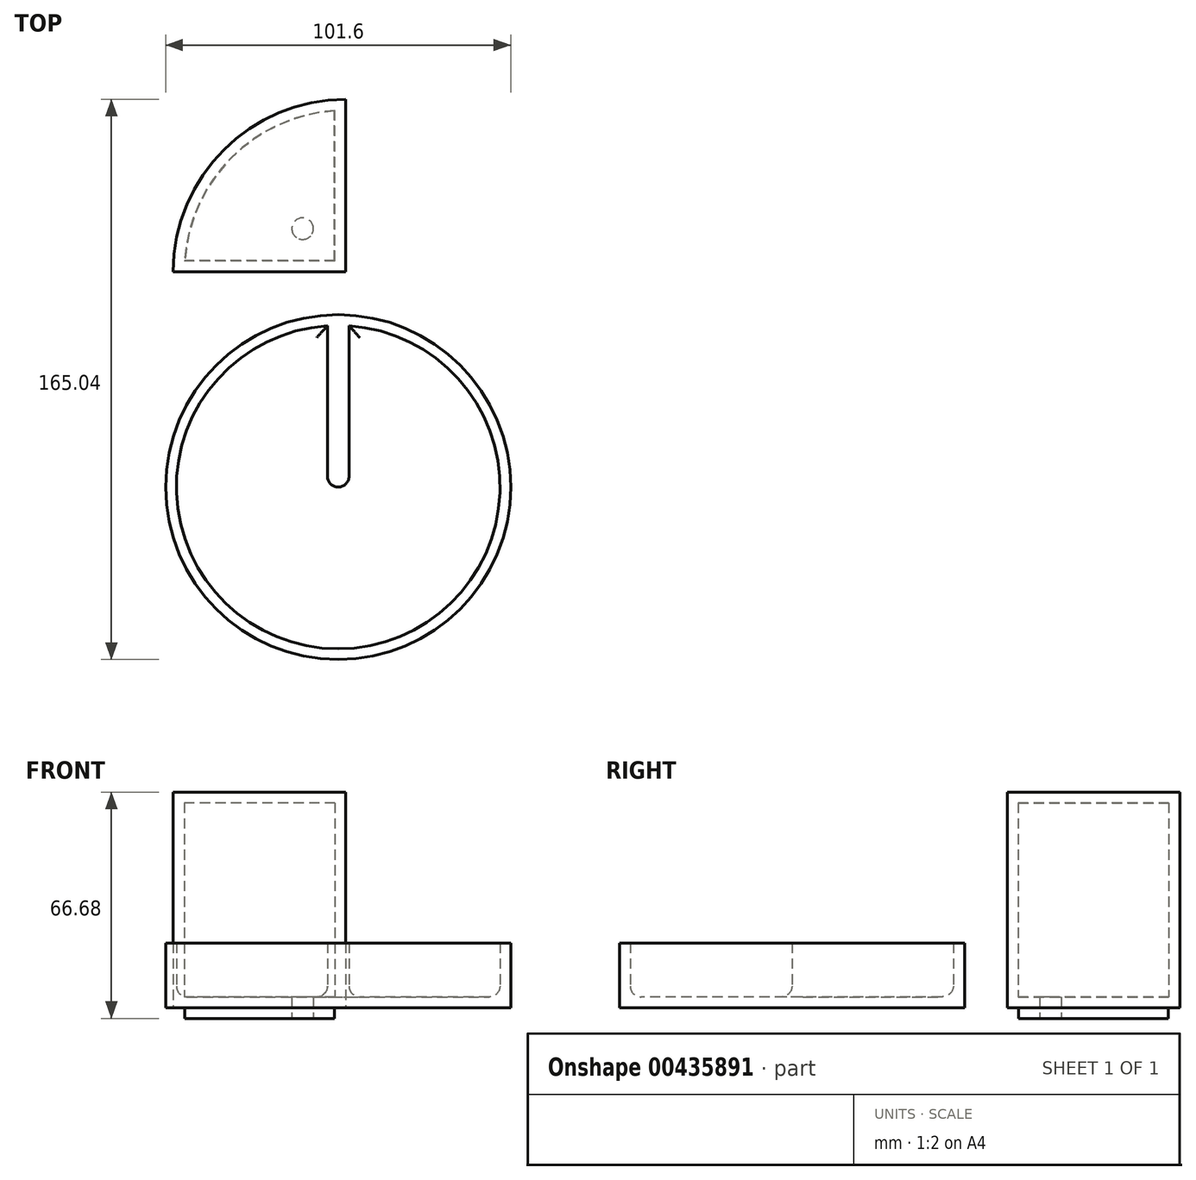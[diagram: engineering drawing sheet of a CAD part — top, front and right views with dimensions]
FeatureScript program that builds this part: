
annotation { "Feature Type Name" : "Feature", "Feature Type Description" : "" }
export const myFeature = defineFeature(function(context is Context, id is Id, definition is map)
    precondition{}
    {
        {
            var Q0;
            Q0=qCreatedBy(makeId("Top.planeOp"),FACE);
            var sketch = newSketch(context, id + "F0", { "sketchPlane" : qUnion([Q0])});
            skCircle(sketch, "E0", {"center": v(0, 0) * mm, "radius": 50.8 * mm});
            skSolve(sketch);
        }
        {
            var Q0;
            Q0 = qSketchRegion(id + "F0", true);
            extrude(context, id + "F1", {"entities" : qUnion([Q0]), "depth" : 19.05 * mm});
        }
        {
            var Q0;
            Q0=makeQuery(id+"F1.opExtrude","CAP_FACE",FACE,{"disambiguationData":[OSD([sQuery(id+"F0.wireOp",EDGE,"E0")])],"isStart":false});
            shell(context, id + "F2", {"entities" : qUnion([Q0]), "thickness" : 3.17 * mm});
        }
        {
            var Q0;
            {var subQ0=sQuery(id+"F0.wireOp",EDGE,"E0");Q0=makeQuery(id+"F2.opShell","OFFSET_FACE",FACE,{"disambiguationData":[OSD([subQ0]),TDD([makeQuery(id+"F1.opExtrude","CAP_FACE",FACE,{"disambiguationData":[OSD([subQ0])],"isStart":true})])]});}
            var sketch = newSketch(context, id + "F3", { "sketchPlane" : qUnion([Q0])});
            skLineSegment(sketch, "E1", {"start": v(0, 0) * mm, "end": v(3.18, 0) * mm});
            skLineSegment(sketch, "E2", {"start": v(3.18, 0) * mm, "end": v(3.18, 47.52) * mm});
            skLineSegment(sketch, "E3.MirrorCS", {"start": v(-3.18, 0) * mm, "end": v(-3.18, 47.52) * mm});
            skLineSegment(sketch, "E4.MirrorCS", {"start": v(0, 0) * mm, "end": v(-3.18, 0) * mm});
            skSolve(sketch);
        }
        {
            var Q0;
            Q0=makeQuery(id+"F3.imprint","IMPRINT",FACE,{"disambiguationData":[TD([[makeQuery(id+"F3.imprint","IMPRINT",EDGE,{"derivedFrom":sQuery(id+"F3.wireOp",EDGE,"E1")}),1.0]])]});
            var Q1;
            Q1=makeQuery(id+"F1.opExtrude","CAP_FACE",FACE,{"disambiguationData":[OSD([sQuery(id+"F0.wireOp",EDGE,"E0")])],"isStart":false});
            extrude(context, id + "F4", {"entities" : qUnion([Q0]), "operationType" : NewBodyOperationType.ADD, "endBound" : BoundingType.UP_TO_SURFACE, "endBoundEntityFace" : qUnion([Q1]), "depth" : 16 * mm});
        }
        {
            var Q0;
            {var subQ0=sQuery(id+"F0.wireOp",EDGE,"E0");Q0=makeQuery(id+"F2.opShell","OFFSET_EDGE",EDGE,{"disambiguationData":[OSD([subQ0]),TDD([makeQuery(id+"F1.opExtrude","CAP_EDGE",EDGE,{"disambiguationData":[OSD([subQ0])],"isStart":true})])]});}
            var Q1;
            Q1=makeQuery(id+"F4.opExtrude","CAP_EDGE",EDGE,{"disambiguationData":[OSD([sQuery(id+"F3.wireOp",EDGE,"E3.MirrorCS")])],"isStart":true});
            var Q2;
            Q2=makeQuery(id+"F4.opExtrude","CAP_EDGE",EDGE,{"disambiguationData":[OSD([sQuery(id+"F3.wireOp",EDGE,"E1"),sQuery(id+"F3.wireOp",EDGE,"E4.MirrorCS")])],"isStart":true});
            var Q3;
            Q3=makeQuery(id+"F4.opExtrude","CAP_EDGE",EDGE,{"disambiguationData":[OSD([sQuery(id+"F3.wireOp",EDGE,"E2")])],"isStart":true});
            var Q4;
            {var subQ0=sQuery(id+"F0.wireOp",EDGE,"E0");Q4=makeQuery(id+"F2.opShell","OFFSET_FACE",FACE,{"disambiguationData":[OSD([subQ0]),TDD([makeQuery(id+"F1.opExtrude","CAP_FACE",FACE,{"disambiguationData":[OSD([subQ0])],"isStart":true})])]});}
            var Q5;
            Q5=makeQuery(id+"F4.opExtrude","SWEPT_EDGE",EDGE,{"disambiguationData":[OSD([sQuery(id+"F3.wireOp",EDGE,"E1"),sQuery(id+"F3.wireOp",EDGE,"E2")])]});
            var Q6;
            Q6=makeQuery(id+"F4.opExtrude","SWEPT_EDGE",EDGE,{"disambiguationData":[OSD([sQuery(id+"F3.wireOp",EDGE,"E3.MirrorCS"),sQuery(id+"F3.wireOp",EDGE,"E4.MirrorCS")])]});
            fillet(context, id + "F5", {"entities" : qUnion([Q0, Q1, Q2, Q3, Q4, Q5, Q6]), "radius" : 3.17 * mm, "tangentPropagation" : true, "allowEdgeOverflow" : false});
        }
        {
            var Q0;
            Q0=qCreatedBy(makeId("Top.planeOp"),FACE);
            var sketch = newSketch(context, id + "F6", { "sketchPlane" : qUnion([Q0])});
            skLineSegment(sketch, "E5", {"start": v(2.24, 63.44) * mm, "end": v(-48.56, 63.44) * mm});
            skLineSegment(sketch, "E6", {"start": v(2.24, 63.44) * mm, "end": v(2.24, 114.24) * mm});
            skArc(sketch, "E7", {"start": v(2.24, 114.24) * mm, "mid": v(-33.68, 99.36) * mm, "end": v(-48.56, 63.44) * mm});
            skSolve(sketch);
        }
        {
            var Q0;
            Q0 = qSketchRegion(id + "F6", true);
            extrude(context, id + "F7", {"entities" : qUnion([Q0]), "depth" : 63.5 * mm});
        }
        {
            var Q0;
            Q0=makeQuery(id+"F7.opExtrude","CAP_FACE",FACE,{"disambiguationData":[OSD([sQuery(id+"F6.wireOp",EDGE,"E5"),sQuery(id+"F6.wireOp",EDGE,"E6"),sQuery(id+"F6.wireOp",EDGE,"E7")])],"isStart":true});
            var Q1;
            Q1=makeQuery(id+"F7.opExtrude","SWEPT_BODY",BODY,{"disambiguationData":[OSD([sQuery(id+"F6.wireOp",EDGE,"E5"),sQuery(id+"F6.wireOp",EDGE,"E6"),sQuery(id+"F6.wireOp",EDGE,"E7")])]});
            shell(context, id + "F8", {"isHollow" : true, "entities" : qUnion([Q0]), "parts" : qUnion([Q1]), "thickness" : 3.17 * mm});
        }
        {
            var Q0;
            Q0=makeQuery(id+"F7.opExtrude","CAP_FACE",FACE,{"disambiguationData":[OSD([sQuery(id+"F6.wireOp",EDGE,"E5"),sQuery(id+"F6.wireOp",EDGE,"E6"),sQuery(id+"F6.wireOp",EDGE,"E7")])],"isStart":true});
            var sketch = newSketch(context, id + "F9", { "sketchPlane" : qUnion([Q0])});
            skLineSegment(sketch, "E8.0", {"start": v(-1.06, -66.75) * mm, "end": v(-45.14, -66.75) * mm});
            skLineSegment(sketch, "E8.1", {"start": v(-1.06, -66.75) * mm, "end": v(-1.06, -110.83) * mm});
            skArc(sketch, "E8.2", {"start": v(-1.06, -110.83) * mm, "mid": v(-31.35, -97.03) * mm, "end": v(-45.14, -66.75) * mm});
            skSolve(sketch);
        }
        {
            var Q0;
            Q0 = qSketchRegion(id + "F9", true);
            extrude(context, id + "F10", {"entities" : qUnion([Q0]), "operationType" : NewBodyOperationType.ADD, "depth" : 3.17 * mm});
        }
        {
            var Q0;
            Q0=makeQuery(id+"F10.opExtrude","CAP_FACE",FACE,{"disambiguationData":[OSD([sQuery(id+"F9.wireOp",EDGE,"E8.0"),sQuery(id+"F9.wireOp",EDGE,"E8.1"),sQuery(id+"F9.wireOp",EDGE,"E8.2")])],"isStart":false});
            var sketch = newSketch(context, id + "F11", { "sketchPlane" : qUnion([Q0])});
            skCircle(sketch, "E9", {"center": v(-10.46, -76.14) * mm, "radius": 3.18 * mm});
            skSolve(sketch);
        }
        {
            var Q0;
            Q0 = qSketchRegion(id + "F11", true);
            extrude(context, id + "F12", {"entities" : qUnion([Q0]), "operationType" : NewBodyOperationType.REMOVE, "oppositeDirection" : true, "depth" : 25.4 * mm});
        }
    });
